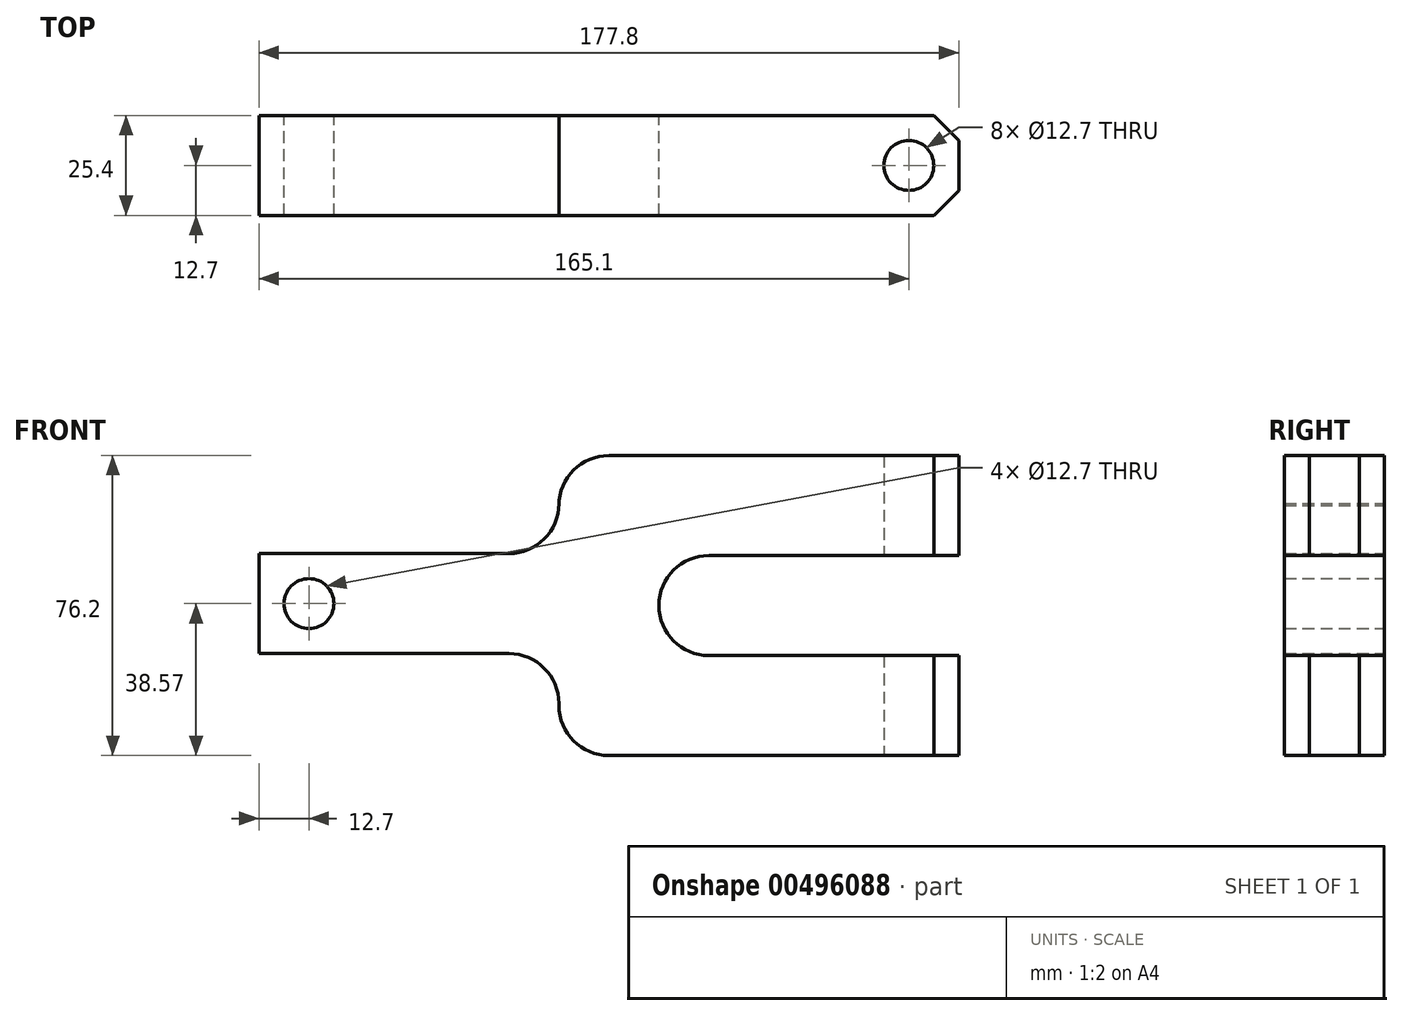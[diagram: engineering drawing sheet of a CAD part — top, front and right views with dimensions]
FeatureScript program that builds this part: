
annotation { "Feature Type Name" : "Feature", "Feature Type Description" : "" }
export const myFeature = defineFeature(function(context is Context, id is Id, definition is map)
    precondition{}
    {
        {
            var Q0;
            Q0=qCreatedBy(makeId("Front.planeOp"),FACE);
            var sketch = newSketch(context, id + "F0", { "sketchPlane" : qUnion([Q0])});
            skLineSegment(sketch, "E0.bottom", {"start": v(-50.8, 12.7) * mm, "end": v(12.7, 12.7) * mm});
            skLineSegment(sketch, "E0.top", {"start": v(-50.8, -12.7) * mm, "end": v(12.7, -12.7) * mm});
            skLineSegment(sketch, "E0.left", {"start": v(-50.8, 12.7) * mm, "end": v(-50.8, -12.7) * mm});
            skLineSegment(sketch, "E0.right", {"start": v(50.8, -0.47) * mm, "end": v(50.8, -0.47) * mm});
            skPoint(sketch, "E0.middle", {"position": v(0, 0) * mm});
            skLineSegment(sketch, "E1.bottom", {"start": v(127, 12.23) * mm, "end": v(63.5, 12.23) * mm});
            skLineSegment(sketch, "E1.top", {"start": v(127, 37.63) * mm, "end": v(38.1, 37.63) * mm});
            skLineSegment(sketch, "E1.left", {"start": v(127, 12.23) * mm, "end": v(127, 37.63) * mm});
            skLineSegment(sketch, "E1.right", {"start": v(25.4, 24.93) * mm, "end": v(25.4, 25.4) * mm});
            skPoint(sketch, "E1.middle", {"position": v(76.2, 24.93) * mm});
            skLineSegment(sketch, "E2.bottom", {"start": v(127, -38.57) * mm, "end": v(38.1, -38.57) * mm});
            skLineSegment(sketch, "E2.top", {"start": v(127, -13.17) * mm, "end": v(63.5, -13.17) * mm});
            skLineSegment(sketch, "E2.left", {"start": v(127, -38.57) * mm, "end": v(127, -13.17) * mm});
            skLineSegment(sketch, "E2.right", {"start": v(25.4, -25.87) * mm, "end": v(25.4, -25.4) * mm});
            skPoint(sketch, "E2.middle", {"position": v(76.2, -25.87) * mm});
            skPoint(sketch, "E3.newPointA", {"position": v(50.8, 12.7) * mm});
            skPoint(sketch, "E3.newPointB", {"position": v(25.4, 12.57) * mm});
            skArc(sketch, "E3.filletArc", {"start": v(12.7, 12.7) * mm, "mid": v(21.68, 16.42) * mm, "end": v(25.4, 25.4) * mm});
            skPoint(sketch, "E4.visualSharp", {"position": v(25.4, 37.63) * mm});
            skArc(sketch, "E4.filletArc", {"start": v(38.1, 37.63) * mm, "mid": v(29.12, 33.91) * mm, "end": v(25.4, 24.93) * mm});
            skPoint(sketch, "E5.newPointA", {"position": v(50.8, -12.7) * mm});
            skPoint(sketch, "E5.newPointB", {"position": v(25.4, -13.17) * mm});
            skArc(sketch, "E5.filletArc", {"start": v(25.4, -25.4) * mm, "mid": v(21.68, -16.42) * mm, "end": v(12.7, -12.7) * mm});
            skPoint(sketch, "E6.visualSharp", {"position": v(25.4, -38.57) * mm});
            skArc(sketch, "E6.filletArc", {"start": v(25.4, -25.87) * mm, "mid": v(29.12, -34.85) * mm, "end": v(38.1, -38.57) * mm});
            skPoint(sketch, "E7.newPointA", {"position": v(25.4, 12.23) * mm});
            skArc(sketch, "E7.filletArc", {"start": v(63.5, 12.23) * mm, "mid": v(54.52, 8.51) * mm, "end": v(50.8, -0.47) * mm});
            skArc(sketch, "E8.filletArc", {"start": v(50.8, -0.47) * mm, "mid": v(54.52, -9.45) * mm, "end": v(63.5, -13.17) * mm});
            skCircle(sketch, "E9", {"center": v(-38.1, 0) * mm, "radius": 6.35 * mm});
            skSolve(sketch);
        }
        {
            var Q0;
            Q0=makeQuery(id+"F0.imprint","IMPRINT",FACE,{"disambiguationData":[TD([[makeQuery(id+"F0.imprint","IMPRINT",EDGE,{"derivedFrom":sQuery(id+"F0.wireOp",EDGE,"E0.bottom")}),-1.0]])]});
            extrude(context, id + "F1", {"entities" : qUnion([Q0]), "depth" : 25.4 * mm});
        }
        {
            var Q0;
            Q0=makeQuery(id+"F1.opExtrude","SWEPT_FACE",FACE,{"disambiguationData":[OSD([sQuery(id+"F0.wireOp",EDGE,"E2.bottom")])]});
            var sketch = newSketch(context, id + "F2", { "sketchPlane" : qUnion([Q0])});
            skCircle(sketch, "E10", {"center": v(114.3, 12.7) * mm, "radius": 6.35 * mm});
            skSolve(sketch);
        }
        {
            var Q0;
            Q0=sQuery(id+"F2.wireOp",VERTEX,"E10.center");
            var Q1;
            Q1=makeQuery(id+"F1.opExtrude","SWEPT_BODY",BODY,{"disambiguationData":[OSD([sQuery(id+"F0.wireOp",EDGE,"E0.bottom"),sQuery(id+"F0.wireOp",EDGE,"E0.top"),sQuery(id+"F0.wireOp",EDGE,"E0.left"),sQuery(id+"F0.wireOp",EDGE,"E1.bottom"),sQuery(id+"F0.wireOp",EDGE,"E1.top"),sQuery(id+"F0.wireOp",EDGE,"E1.left"),sQuery(id+"F0.wireOp",EDGE,"E1.right"),sQuery(id+"F0.wireOp",EDGE,"E2.bottom"),sQuery(id+"F0.wireOp",EDGE,"E2.top"),sQuery(id+"F0.wireOp",EDGE,"E2.left"),sQuery(id+"F0.wireOp",EDGE,"E2.right"),sQuery(id+"F0.wireOp",EDGE,"E3.filletArc"),sQuery(id+"F0.wireOp",EDGE,"E4.filletArc"),sQuery(id+"F0.wireOp",EDGE,"E5.filletArc"),sQuery(id+"F0.wireOp",EDGE,"E6.filletArc"),sQuery(id+"F0.wireOp",EDGE,"E7.filletArc"),sQuery(id+"F0.wireOp",EDGE,"E8.filletArc"),sQuery(id+"F0.wireOp",EDGE,"E9")])]});
            hole(context, id + "F3", {"style" : HoleStyle.SIMPLE, "endStyle" : HoleEndStyle.THROUGH, "holeDiameter" : 12.7 * mm, "isTappedThrough" : true, "tappedDepth" : 12.7 * mm, "tapClearance" : 3, "locations" : qUnion([Q0]), "scope" : qUnion([Q1])});
        }
        {
            var Q0;
            Q0=makeQuery(id+"F1.opExtrude","CAP_EDGE",EDGE,{"disambiguationData":[OSD([sQuery(id+"F0.wireOp",EDGE,"E2.left")])],"isStart":false});
            var Q1;
            Q1=makeQuery(id+"F1.opExtrude","CAP_EDGE",EDGE,{"disambiguationData":[OSD([sQuery(id+"F0.wireOp",EDGE,"E2.left")])],"isStart":true});
            var Q2;
            Q2=makeQuery(id+"F1.opExtrude","CAP_EDGE",EDGE,{"disambiguationData":[OSD([sQuery(id+"F0.wireOp",EDGE,"E1.left")])],"isStart":false});
            var Q3;
            Q3=makeQuery(id+"F1.opExtrude","CAP_EDGE",EDGE,{"disambiguationData":[OSD([sQuery(id+"F0.wireOp",EDGE,"E1.left")])],"isStart":true});
            chamfer(context, id + "F4", {"entities" : qUnion([Q0, Q1, Q2, Q3]), "width" : 6.35 * mm, "tangentPropagation" : true});
        }
    });
